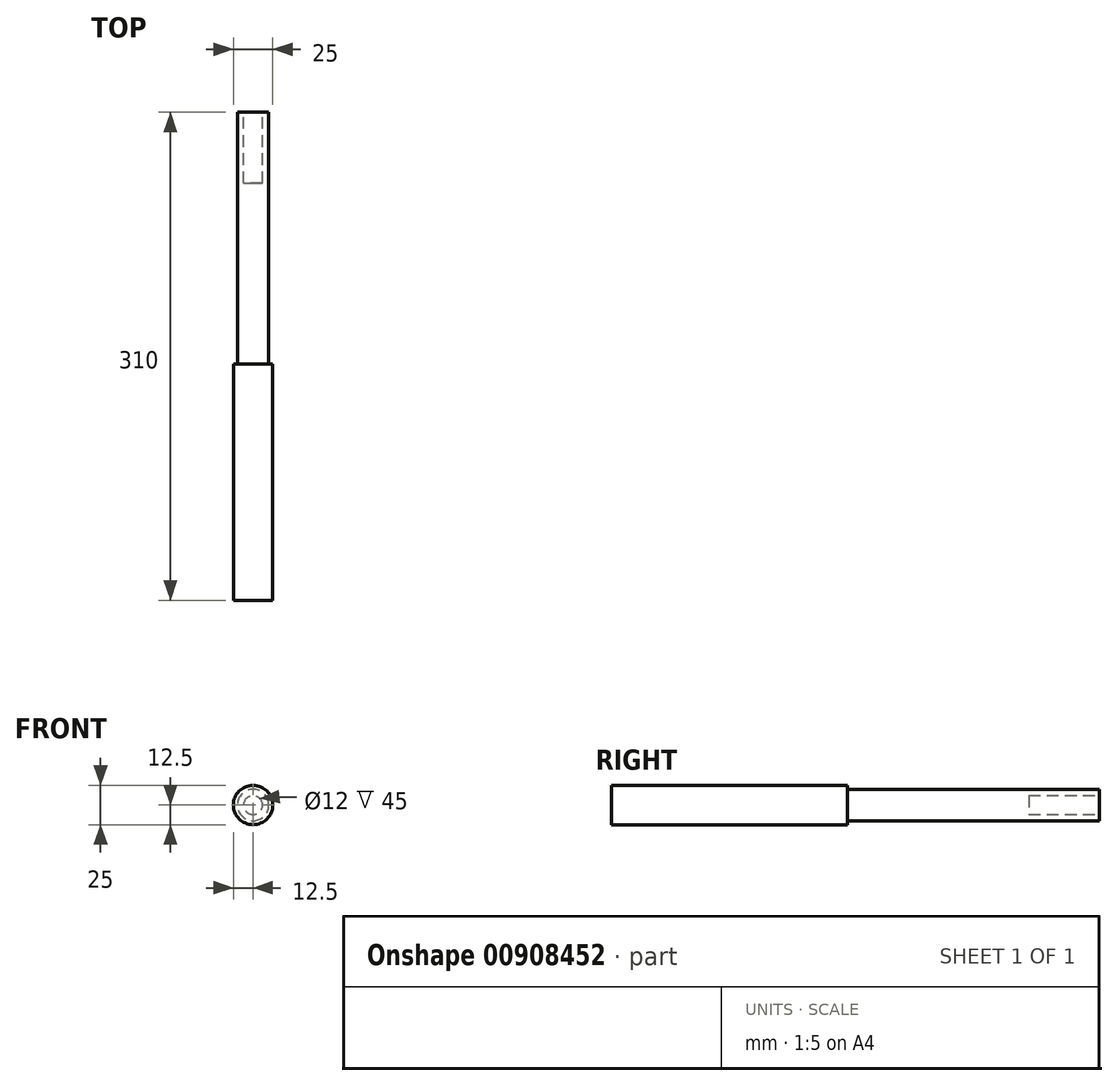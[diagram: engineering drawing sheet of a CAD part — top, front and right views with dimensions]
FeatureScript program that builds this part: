
annotation { "Feature Type Name" : "Feature", "Feature Type Description" : "" }
export const myFeature = defineFeature(function(context is Context, id is Id, definition is map)
    precondition{}
    {
        {
            var Q0;
            Q0=qCreatedBy(makeId("Front.planeOp"),FACE);
            var sketch = newSketch(context, id + "F0", { "sketchPlane" : qUnion([Q0])});
            skCircle(sketch, "E0", {"center": v(0, 0) * mm, "radius": 12.5 * mm});
            skSolve(sketch);
        }
        {
            var Q0;
            Q0 = qSketchRegion(id + "F0", true);
            extrude(context, id + "F1", {"entities" : qUnion([Q0]), "depth" : 310 * mm, "offsetDistance" : 25 * mm});
        }
        {
            var Q0;
            Q0=makeQuery(id+"F1.opExtrude","CAP_FACE",FACE,{"disambiguationData":[OSD([sQuery(id+"F0.wireOp",EDGE,"E0")])],"isStart":true});
            var sketch = newSketch(context, id + "F2", { "sketchPlane" : qUnion([Q0])});
            skCircle(sketch, "E1", {"center": v(0, 0) * mm, "radius": 6 * mm});
            skSolve(sketch);
        }
        {
            var Q0;
            Q0 = qSketchRegion(id + "F2", true);
            extrude(context, id + "F3", {"entities" : qUnion([Q0]), "operationType" : NewBodyOperationType.REMOVE, "oppositeDirection" : true, "depth" : 45 * mm, "offsetDistance" : 25 * mm});
        }
        {
            var Q0;
            Q0=makeQuery(id+"F1.opExtrude","CAP_EDGE",EDGE,{"disambiguationData":[OSD([sQuery(id+"F0.wireOp",EDGE,"E0")])],"isStart":true});
            chamfer(context, id + "F4", {"entities" : qUnion([Q0]), "width" : 1 * mm, "tangentPropagation" : true});
        }
        {
            var Q0;
            Q0=qCreatedBy(makeId("Front.planeOp"),FACE);
            var sketch = newSketch(context, id + "F5", { "sketchPlane" : qUnion([Q0])});
            skCircle(sketch, "E2", {"center": v(0, 0) * mm, "radius": 10 * mm});
            skCircle(sketch, "E3", {"center": v(0, 0) * mm, "radius": 20.96 * mm});
            skSolve(sketch);
        }
        {
            var Q0;
            Q0 = qSketchRegion(id + "F5", true);
            extrude(context, id + "F6", {"entities" : qUnion([Q0]), "operationType" : NewBodyOperationType.REMOVE, "depth" : 160 * mm, "offsetDistance" : 25 * mm});
        }
    });
